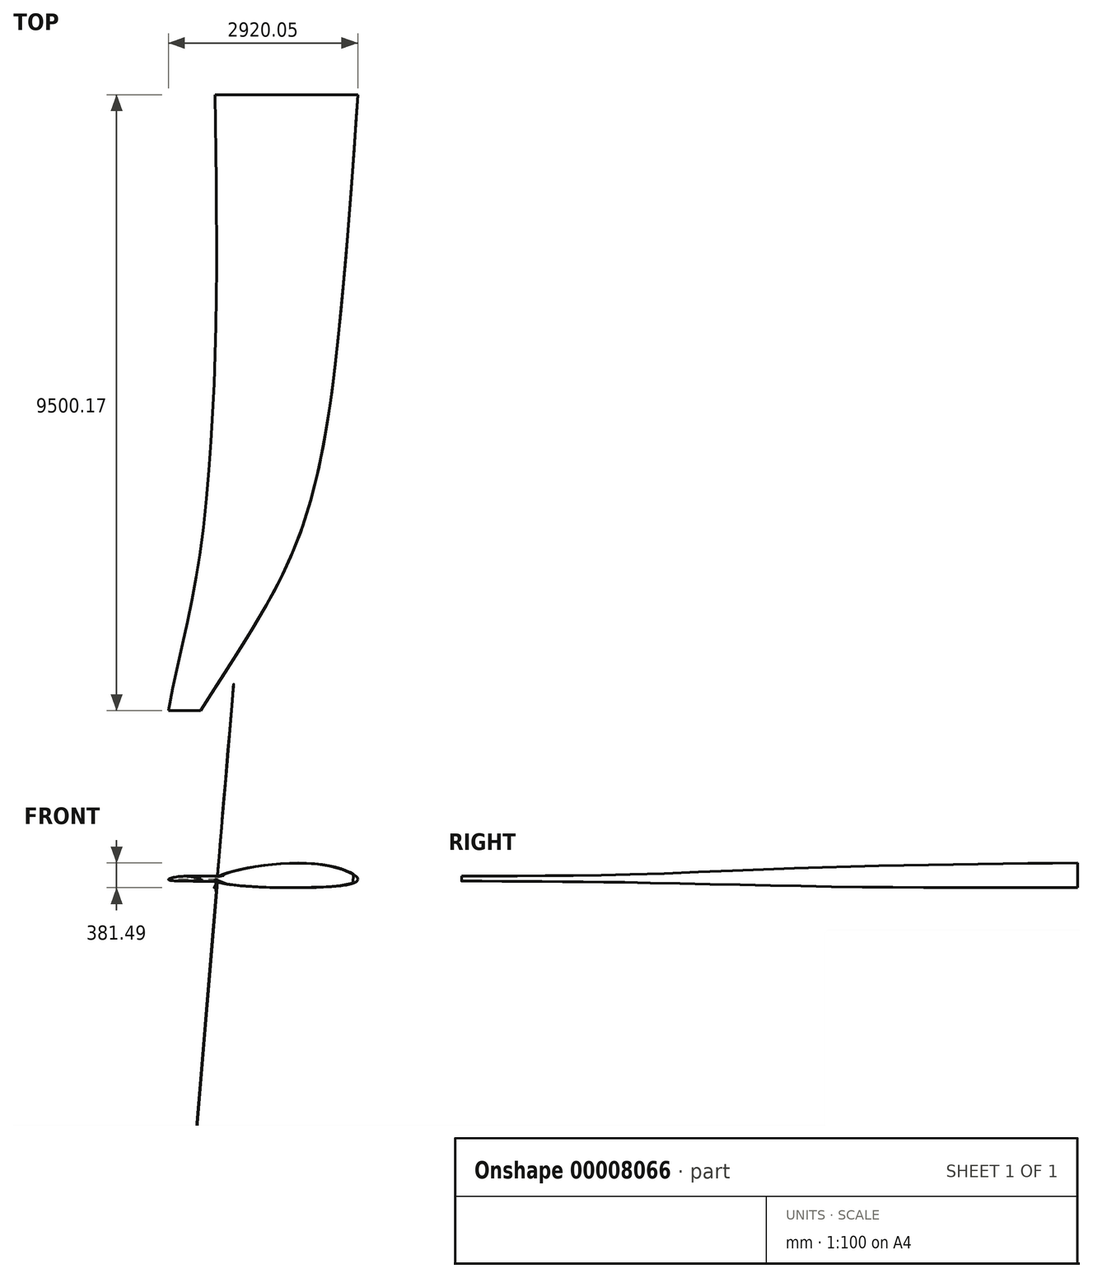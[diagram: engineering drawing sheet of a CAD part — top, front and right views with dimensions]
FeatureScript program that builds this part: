
annotation { "Feature Type Name" : "Feature", "Feature Type Description" : "" }
export const myFeature = defineFeature(function(context is Context, id is Id, definition is map)
    precondition{}
    {
        {
            var Q0;
            Q0=qCreatedBy(makeId("Front.planeOp"),FACE);
            var sketch = newSketch(context, id + "F0", { "sketchPlane" : qUnion([Q0])});
            skLineSegment(sketch, "E0", {"start": v(0, -125) * mm, "end": v(0, 250) * mm, "construction": true});
            skPoint(sketch, "E1", {"position": v(-1440, 0) * mm});
            skPoint(sketch, "E2", {"position": v(760, 0) * mm});
            skFitSpline(sketch, "E3", {"points": [v(-1440, 0) * mm, v(0, 250) * mm, v(760, 0) * mm, v(0, -125) * mm, v(-1440, 0) * mm]});
            skSolve(sketch);
        }
        {
            var Q0;
            Q0=makeQuery(id+"F0.imprint","IMPRINT",FACE,{"disambiguationData":[TD([[makeQuery(id+"F0.imprint","IMPRINT",EDGE,{"derivedFrom":sQuery(id+"F0.wireOp",EDGE,"E3")}),-1.0]])]});
            cPlane(context, id + "F1", {"entities" : qUnion([Q0]), "cplaneType" : CPlaneType.OFFSET, "offset" : 4000 * mm, "width" : 150 * mm, "height" : 150 * mm});
        }
        {
            var Q0;
            Q0=qCreatedBy(id+"F1.planeOp",FACE);
            cPlane(context, id + "F2", {"entities" : qUnion([Q0]), "cplaneType" : CPlaneType.OFFSET, "offset" : 3000 * mm, "width" : 150 * mm, "height" : 150 * mm});
        }
        {
            var Q0;
            Q0=qCreatedBy(id+"F1.planeOp",FACE);
            var sketch = newSketch(context, id + "F3", { "sketchPlane" : qUnion([Q0])});
            skLineSegment(sketch, "E4", {"start": v(0, 0) * mm, "end": v(-1440, 0) * mm, "construction": true});
            skLineSegment(sketch, "E5", {"start": v(0, 0) * mm, "end": v(430, 0) * mm, "construction": true});
            skLineSegment(sketch, "E6", {"start": v(0, 0) * mm, "end": v(0, 175) * mm, "construction": true});
            skLineSegment(sketch, "E7", {"start": v(0, 0) * mm, "end": v(0, -100) * mm, "construction": true});
            skFitSpline(sketch, "E8", {"points": [v(-1440, 0) * mm, v(0, 175) * mm, v(430, 0) * mm, v(0, -100) * mm, v(-1440, 0) * mm]});
            skSolve(sketch);
        }
        {
            var Q0;
            Q0=qCreatedBy(id+"F2.planeOp",FACE);
            var sketch = newSketch(context, id + "F4", { "sketchPlane" : qUnion([Q0])});
            skLineSegment(sketch, "E9", {"start": v(-1660, 0) * mm, "end": v(-220, 0) * mm, "construction": true});
            skPoint(sketch, "E10", {"position": v(-940, 0) * mm});
            skLineSegment(sketch, "E11", {"start": v(-940, 0) * mm, "end": v(-940, 75) * mm, "construction": true});
            skLineSegment(sketch, "E12", {"start": v(-940, 0) * mm, "end": v(-940, -45) * mm, "construction": true});
            skFitSpline(sketch, "E13", {"points": [v(-1660, 0) * mm, v(-940, 75) * mm, v(-220, 0) * mm, v(-940, -45) * mm, v(-1660, 0) * mm]});
            skSolve(sketch);
        }
        {
            var Q0;
            Q0=qCreatedBy(id+"F2.planeOp",FACE);
            cPlane(context, id + "F5", {"entities" : qUnion([Q0]), "cplaneType" : CPlaneType.OFFSET, "offset" : 2500 * mm, "width" : 150 * mm, "height" : 150 * mm});
        }
        {
            var Q0;
            Q0=qCreatedBy(id+"F5.planeOp",FACE);
            var sketch = newSketch(context, id + "F6", { "sketchPlane" : qUnion([Q0])});
            skLineSegment(sketch, "E14", {"start": v(-2160, 0) * mm, "end": v(-1660, 0) * mm, "construction": true});
            skLineSegment(sketch, "E15", {"start": v(-1910, 0) * mm, "end": v(-1910, 50) * mm, "construction": true});
            skLineSegment(sketch, "E16", {"start": v(-1910, 0) * mm, "end": v(-1910, -25) * mm, "construction": true});
            skFitSpline(sketch, "E17", {"points": [v(-2160, 0) * mm, v(-1910, 50) * mm, v(-1660, 0) * mm, v(-1910, -25) * mm, v(-2160, 0) * mm]});
            skSolve(sketch);
        }
        {
            var Q0;
            Q0=qCreatedBy(makeId("Top.planeOp"),FACE);
            var sketch = newSketch(context, id + "F7", { "sketchPlane" : qUnion([Q0])});
            skPoint(sketch, "E18", {"position": v(760, 0) * mm});
            skPoint(sketch, "E19", {"position": v(430, -4000) * mm});
            skPoint(sketch, "E20", {"position": v(-220, -7000) * mm});
            skPoint(sketch, "E21", {"position": v(-1660, -9500) * mm});
            skFitSpline(sketch, "E22", {"points": [v(760, 0) * mm, v(430, -4000) * mm, v(-220, -7000) * mm, v(-1660, -9500) * mm], "startDerivative": vector(-744.8, -11209.75) * mm, "endDerivative": vector(-4861.61, -7845.53) * mm});
            skSolve(sketch);
        }
        {
            var Q0;
            Q0=makeQuery(id+"F0.imprint","IMPRINT",FACE,{"disambiguationData":[TD([[makeQuery(id+"F0.imprint","IMPRINT",EDGE,{"derivedFrom":sQuery(id+"F0.wireOp",EDGE,"E3")}),-1.0]])]});
            var Q1;
            Q1=makeQuery(id+"F3.imprint","IMPRINT",FACE,{"disambiguationData":[TD([[makeQuery(id+"F3.imprint","IMPRINT",EDGE,{"derivedFrom":sQuery(id+"F3.wireOp",EDGE,"E8")}),-1.0]])]});
            var Q2;
            Q2=makeQuery(id+"F4.imprint","IMPRINT",FACE,{"disambiguationData":[TD([[makeQuery(id+"F4.imprint","IMPRINT",EDGE,{"derivedFrom":sQuery(id+"F4.wireOp",EDGE,"E13")}),-1.0]])]});
            var Q3;
            Q3=makeQuery(id+"F6.imprint","IMPRINT",FACE,{"disambiguationData":[TD([[makeQuery(id+"F6.imprint","IMPRINT",EDGE,{"derivedFrom":sQuery(id+"F6.wireOp",EDGE,"E17")}),-1.0]])]});
            var Q4;
            Q4=sQuery(id+"F7.wireOp",EDGE,"E22");
            loft(context, id + "F8", {"addGuides" : true, "sheetProfilesArray" : [{ "sheetProfileEntities" : qUnion([Q0]) }, { "sheetProfileEntities" : qUnion([Q1]) }, { "sheetProfileEntities" : qUnion([Q2]) }, { "sheetProfileEntities" : qUnion([Q3]) }], "guidesArray" : [{ "guideEntities" : qUnion([Q4]), "guideDerivativeType" : LoftGuideDerivativeType.DEFAULT, "guideDerivativeMagnitude" : 1 }]});
        }
        {
            var Q0;
            Q0=makeQuery(id+"F8.opLoft","CAP_FACE",FACE,{"disambiguationData":[OSD([makeQuery(id+"F0.imprint","IMPRINT",FACE,{"disambiguationData":[TD([[makeQuery(id+"F0.imprint","IMPRINT",EDGE,{"derivedFrom":sQuery(id+"F0.wireOp",EDGE,"E3")}),-1.0]])]})])],"isStart":true});
            shell(context, id + "F9", {"entities" : qUnion([Q0]), "thickness" : 2.5 * mm});
        }
    });
